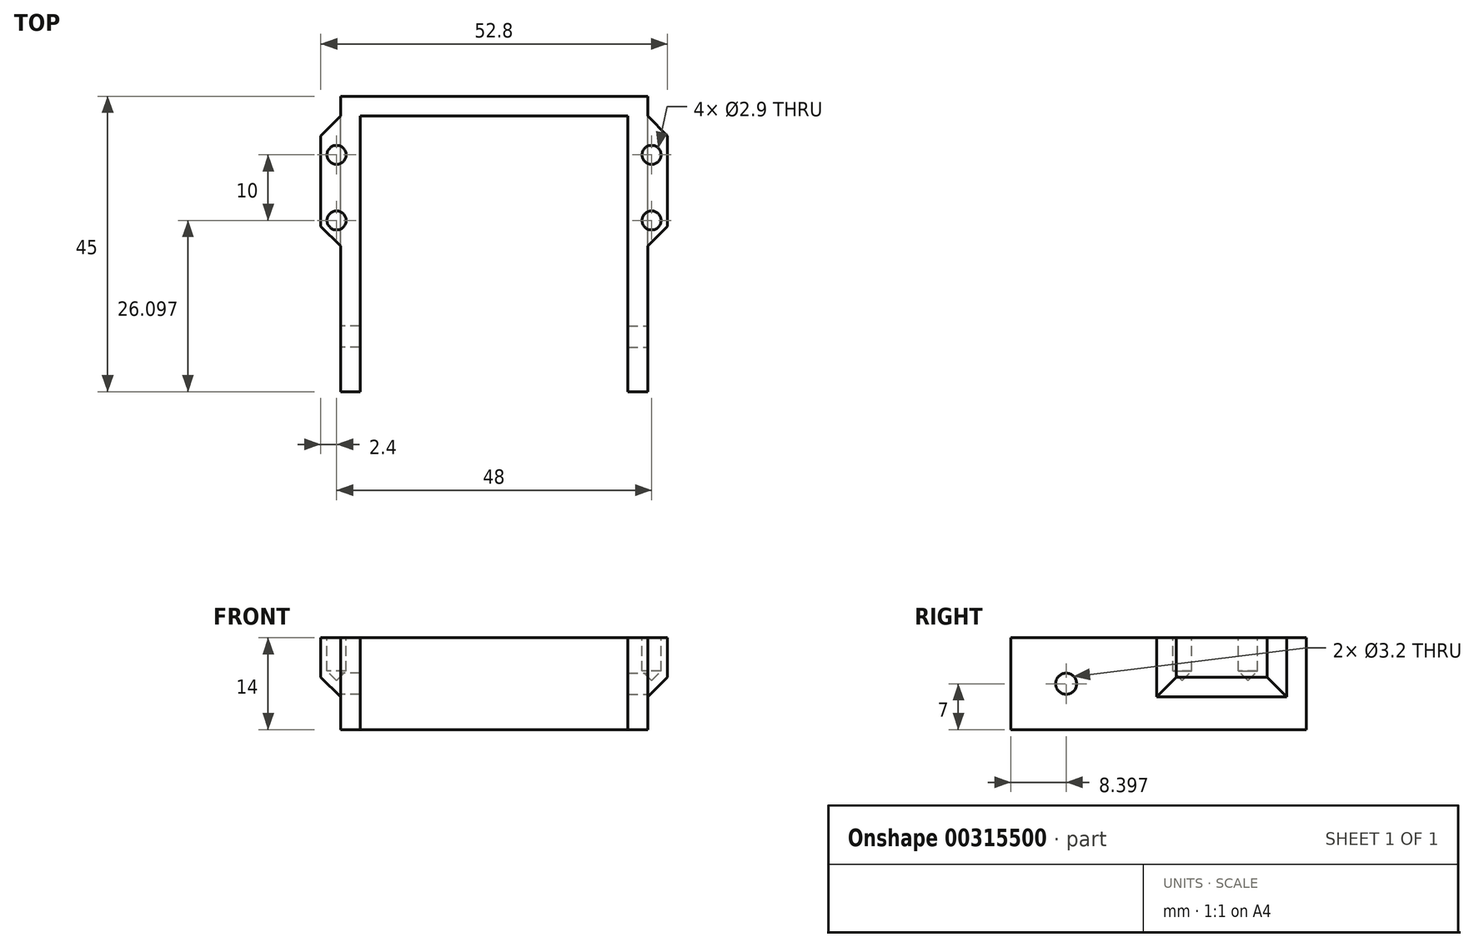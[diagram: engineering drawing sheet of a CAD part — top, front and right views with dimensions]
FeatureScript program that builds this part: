
annotation { "Feature Type Name" : "Feature", "Feature Type Description" : "" }
export const myFeature = defineFeature(function(context is Context, id is Id, definition is map)
    precondition{}
    {
        {
            var Q0;
            Q0=qCreatedBy(makeId("Top.planeOp"),FACE);
            var sketch = newSketch(context, id + "F0", { "sketchPlane" : qUnion([Q0])});
            skLineSegment(sketch, "E0", {"start": v(0, 21.27) * mm, "end": v(20.4, 21.27) * mm});
            skLineSegment(sketch, "E1", {"start": v(20.4, 21.27) * mm, "end": v(20.4, -20.73) * mm});
            skLineSegment(sketch, "E2", {"start": v(20.4, -20.73) * mm, "end": v(23.4, -20.73) * mm});
            skLineSegment(sketch, "E3", {"start": v(23.4, -20.73) * mm, "end": v(23.4, 24.27) * mm});
            skLineSegment(sketch, "E4", {"start": v(23.4, 24.27) * mm, "end": v(0, 24.27) * mm});
            skLineSegment(sketch, "E5", {"start": v(0, 24.27) * mm, "end": v(0, 21.27) * mm});
            skSolve(sketch);
        }
        {
            var Q0;
            Q0 = qSketchRegion(id + "F0", true);
            extrude(context, id + "F1", {"entities" : qUnion([Q0]), "depth" : 14 * mm});
        }
        {
            var Q0;
            Q0=makeQuery(id+"F1.opExtrude","CAP_FACE",FACE,{"disambiguationData":[OSD([sQuery(id+"F0.wireOp",EDGE,"E0"),sQuery(id+"F0.wireOp",EDGE,"E1"),sQuery(id+"F0.wireOp",EDGE,"E2"),sQuery(id+"F0.wireOp",EDGE,"E3"),sQuery(id+"F0.wireOp",EDGE,"E4"),sQuery(id+"F0.wireOp",EDGE,"E5")])],"isStart":false});
            var sketch = newSketch(context, id + "F2", { "sketchPlane" : qUnion([Q0])});
            skLineSegment(sketch, "E6.bottom", {"start": v(20.4, 21.27) * mm, "end": v(26.4, 21.27) * mm});
            skLineSegment(sketch, "E6.top", {"start": v(20.4, 1.47) * mm, "end": v(26.4, 1.47) * mm});
            skLineSegment(sketch, "E6.left", {"start": v(20.4, 21.27) * mm, "end": v(20.4, 1.47) * mm});
            skLineSegment(sketch, "E6.right", {"start": v(26.4, 21.27) * mm, "end": v(26.4, 1.47) * mm});
            skSolve(sketch);
        }
        {
            var Q0;
            Q0 = qSketchRegion(id + "F2", true);
            extrude(context, id + "F3", {"entities" : qUnion([Q0]), "operationType" : NewBodyOperationType.ADD, "oppositeDirection" : true, "depth" : 9 * mm});
        }
        {
            var Q0;
            Q0=makeQuery(id+"F3.boolean.opBoolean","MERGE",FACE,{"derivedFrom":[makeQuery(id+"F1.opExtrude","CAP_FACE",FACE,{"disambiguationData":[OSD([sQuery(id+"F0.wireOp",EDGE,"E0"),sQuery(id+"F0.wireOp",EDGE,"E1"),sQuery(id+"F0.wireOp",EDGE,"E2"),sQuery(id+"F0.wireOp",EDGE,"E3"),sQuery(id+"F0.wireOp",EDGE,"E4"),sQuery(id+"F0.wireOp",EDGE,"E5")])],"isStart":false}),makeQuery(id+"F3.opExtrude","CAP_FACE",FACE,{"disambiguationData":[OSD([sQuery(id+"F2.wireOp",EDGE,"E6.bottom"),sQuery(id+"F2.wireOp",EDGE,"E6.top"),sQuery(id+"F2.wireOp",EDGE,"E6.left"),sQuery(id+"F2.wireOp",EDGE,"E6.right")])],"isStart":true})]});
            var sketch = newSketch(context, id + "F4", { "sketchPlane" : qUnion([Q0])});
            skCircle(sketch, "E7", {"center": v(24, 5.37) * mm, "radius": 1.45 * mm});
            skCircle(sketch, "E8", {"center": v(24, 15.37) * mm, "radius": 1.45 * mm});
            skLineSegment(sketch, "E9", {"start": v(24, 15.37) * mm, "end": v(24, 17.37) * mm, "construction": true});
            skLineSegment(sketch, "E10", {"start": v(24, 17.37) * mm, "end": v(24, 21.27) * mm, "construction": true});
            skLineSegment(sketch, "E11", {"start": v(24, 5.37) * mm, "end": v(24, 1.47) * mm, "construction": true});
            skSolve(sketch);
        }
        {
            var Q0;
            Q0 = qSketchRegion(id + "F4", true);
            extrude(context, id + "F5", {"entities" : qUnion([Q0]), "operationType" : NewBodyOperationType.REMOVE, "oppositeDirection" : true, "depth" : 6.5 * mm});
        }
        {
            var Q0;
            Q0=makeQuery(id+"F3.opExtrude","SWEPT_EDGE",EDGE,{"disambiguationData":[OSD([sQuery(id+"F2.wireOp",EDGE,"E6.top"),sQuery(id+"F2.wireOp",EDGE,"E6.right")])]});
            var Q1;
            Q1=makeQuery(id+"F3.opExtrude","SWEPT_EDGE",EDGE,{"disambiguationData":[OSD([sQuery(id+"F2.wireOp",EDGE,"E6.bottom"),sQuery(id+"F2.wireOp",EDGE,"E6.right")])]});
            var Q2;
            Q2=makeQuery(id+"F3.opExtrude","CAP_EDGE",EDGE,{"disambiguationData":[OSD([sQuery(id+"F2.wireOp",EDGE,"E6.right")])],"isStart":false});
            chamfer(context, id + "F6", {"entities" : qUnion([Q0, Q1, Q2]), "width" : 3 * mm, "tangentPropagation" : true});
        }
        {
            var Q0;
            Q0=makeQuery(id+"F1.opExtrude","SWEPT_FACE",FACE,{"disambiguationData":[OSD([sQuery(id+"F0.wireOp",EDGE,"E3")])]});
            var sketch = newSketch(context, id + "F7", { "sketchPlane" : qUnion([Q0])});
            skCircle(sketch, "E12", {"center": v(-12.33, 7) * mm, "radius": 1.6 * mm});
            skSolve(sketch);
        }
        {
            var Q0;
            Q0 = qSketchRegion(id + "F7", true);
            extrude(context, id + "F8", {"entities" : qUnion([Q0]), "operationType" : NewBodyOperationType.REMOVE, "endBound" : BoundingType.UP_TO_NEXT, "oppositeDirection" : true, "depth" : 25 * mm});
        }
        {
            var Q0;
            Q0=makeQuery(id+"F1.opExtrude","SWEPT_BODY",BODY,{"disambiguationData":[OSD([sQuery(id+"F0.wireOp",EDGE,"E0"),sQuery(id+"F0.wireOp",EDGE,"E1"),sQuery(id+"F0.wireOp",EDGE,"E2"),sQuery(id+"F0.wireOp",EDGE,"E3"),sQuery(id+"F0.wireOp",EDGE,"E4"),sQuery(id+"F0.wireOp",EDGE,"E5")])]});
            var Q1;
            Q1=qCreatedBy(makeId("Right.planeOp"),FACE);
            mirror(context, id + "F9", {"operationType" : NewBodyOperationType.ADD, "entities" : qUnion([Q0]), "mirrorPlane" : qUnion([Q1])});
        }
        {
            var Q0;
            Q0=makeQuery(id+"F5.boolean.opBoolean","COPY",EDGE,{"derivedFrom":makeQuery(id+"F5.opExtrude","CAP_EDGE",EDGE,{"disambiguationData":[OSD([sQuery(id+"F4.wireOp",EDGE,"E8")])],"isStart":false})});
            var Q1;
            Q1=makeQuery(id+"F5.boolean.opBoolean","COPY",FACE,{"derivedFrom":makeQuery(id+"F5.opExtrude","CAP_FACE",FACE,{"disambiguationData":[OSD([sQuery(id+"F4.wireOp",EDGE,"E7")])],"isStart":false})});
            var Q2;
            Q2=makeQuery(id+"F9.opPattern","COPY",EDGE,{"derivedFrom":makeQuery(id+"F5.boolean.opBoolean","COPY",EDGE,{"derivedFrom":makeQuery(id+"F5.opExtrude","CAP_EDGE",EDGE,{"disambiguationData":[OSD([sQuery(id+"F4.wireOp",EDGE,"E7")])],"isStart":false})}),"instanceName":"1"});
            var Q3;
            Q3=makeQuery(id+"F9.opPattern","COPY",EDGE,{"derivedFrom":makeQuery(id+"F5.boolean.opBoolean","COPY",EDGE,{"derivedFrom":makeQuery(id+"F5.opExtrude","CAP_EDGE",EDGE,{"disambiguationData":[OSD([sQuery(id+"F4.wireOp",EDGE,"E8")])],"isStart":false})}),"instanceName":"1"});
            chamfer(context, id + "F10", {"entities" : qUnion([Q0, Q1, Q2, Q3]), "width" : (2.9 / 2) * mm, "tangentPropagation" : true});
        }
    });
